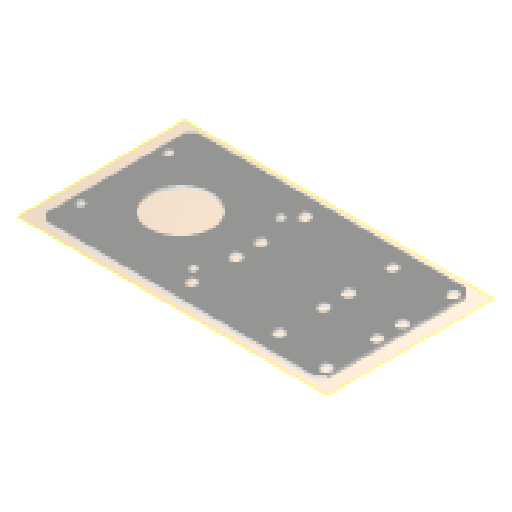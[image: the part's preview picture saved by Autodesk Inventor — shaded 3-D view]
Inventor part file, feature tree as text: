
AUTODESK INVENTOR PART (.ipt)
format: ipt  version: 2024.1 (Build 281209000, 209)  size: 116,736 bytes
history: native  units: mm
features: other x2, plane x1, extrude x1, sketch x1, reference x1
ambient origin geometry x8: Origin, YZ Plane, XZ Plane, XY Plane, X Axis, Y Axis, Z Axis, Center Point
bodies: Volumenkörper1 (feature_tree)
feature tree (6):
  plane  "Arbeitsebene1"
  extrude  "Extrusion1"  [1 undecoded]
  sketch  "Skizze1"  dims[d0=1.0mm d1=0.0mm]
  reference  "Referenz1"
  other  "Assembly_Planktoscope_Uc2version_wormdrive_V3.iam"
  other  "60_Planktoscope_Sampleholder:1"
note: 1 required parameter value undecoded (feature->parameter linkage not recoverable at this tier; creation-order binding heuristic only, values carry confidence <= 0.55)
